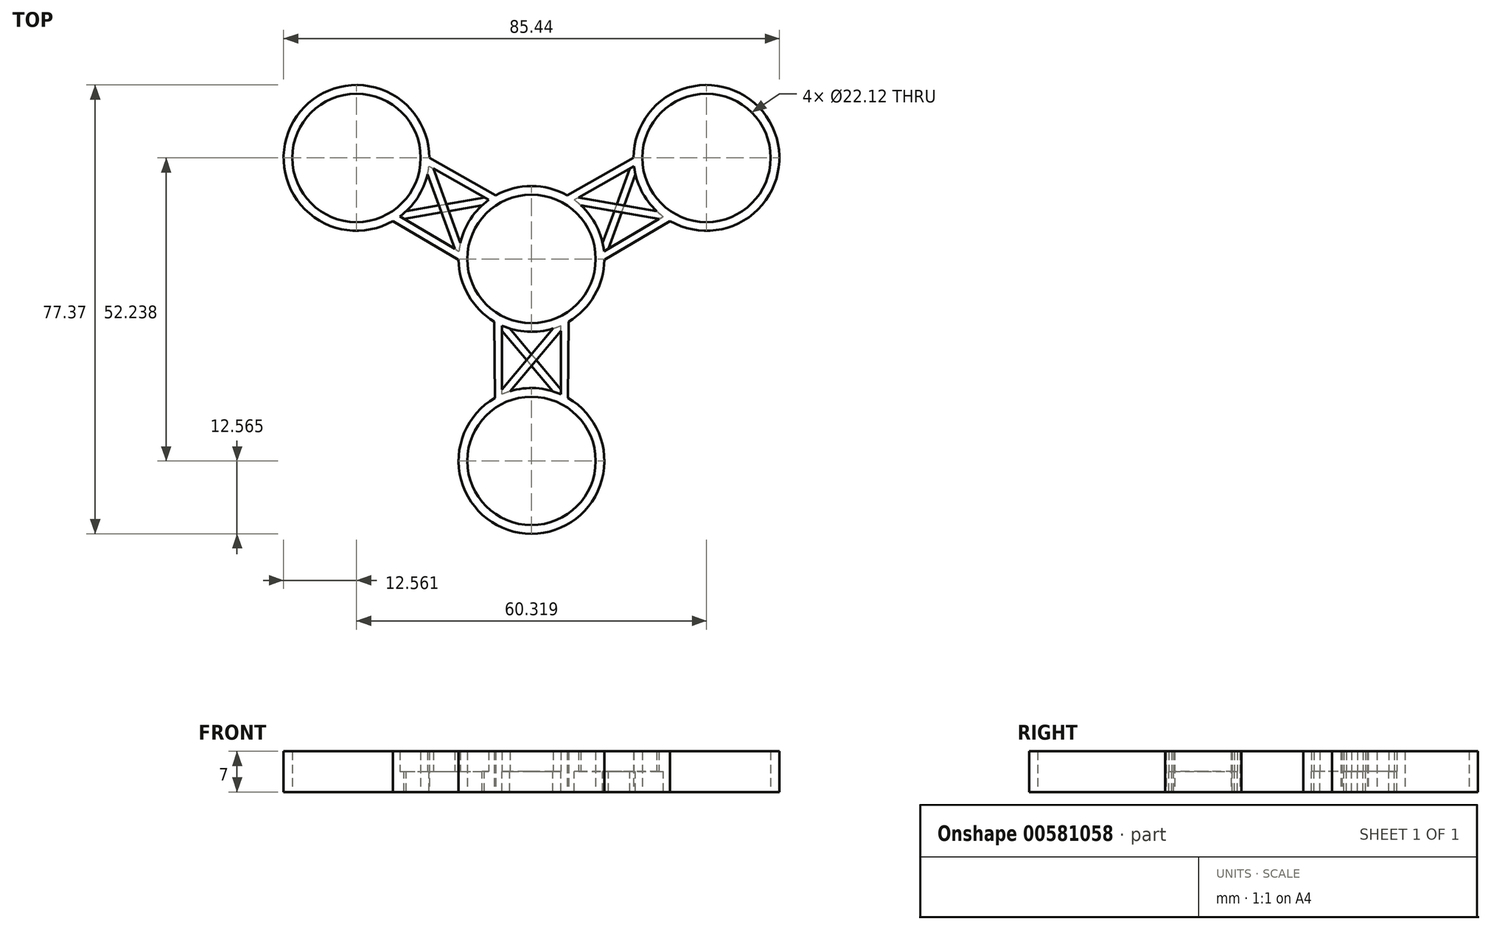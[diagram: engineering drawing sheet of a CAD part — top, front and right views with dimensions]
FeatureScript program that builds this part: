
annotation { "Feature Type Name" : "Feature", "Feature Type Description" : "" }
export const myFeature = defineFeature(function(context is Context, id is Id, definition is map)
    precondition{}
    {
        {
            var Q0;
            Q0=qCreatedBy(makeId("Top.planeOp"),FACE);
            var sketch = newSketch(context, id + "F0", { "sketchPlane" : qUnion([Q0])});
            skCircle(sketch, "E0", {"center": v(0, 0) * mm, "radius": 11.06 * mm});
            skCircle(sketch, "E1", {"center": v(-30.16, 17.41) * mm, "radius": 11.06 * mm});
            skCircle(sketch, "E2", {"center": v(0, -34.82) * mm, "radius": 11.06 * mm});
            skCircle(sketch, "E3", {"center": v(30.16, 17.41) * mm, "radius": 11.06 * mm});
            skLineSegment(sketch, "E4", {"start": v(-30.16, 17.41) * mm, "end": v(0, -34.82) * mm, "construction": true});
            skLineSegment(sketch, "E5", {"start": v(30.16, 17.41) * mm, "end": v(0, -34.82) * mm, "construction": true});
            skLineSegment(sketch, "E6", {"start": v(30.16, 17.41) * mm, "end": v(-30.16, 17.41) * mm, "construction": true});
            skCircle(sketch, "E7", {"center": v(0, 0) * mm, "radius": 12.56 * mm});
            skCircle(sketch, "E8", {"center": v(30.16, 17.41) * mm, "radius": 12.56 * mm});
            skCircle(sketch, "E9", {"center": v(-30.16, 17.41) * mm, "radius": 12.56 * mm});
            skCircle(sketch, "E10", {"center": v(0, -34.82) * mm, "radius": 12.56 * mm});
            skLineSegment(sketch, "E11", {"start": v(3.75, -11.99) * mm, "end": v(-6.28, -23.95) * mm});
            skLineSegment(sketch, "E12", {"start": v(-3.75, -11.99) * mm, "end": v(6.28, -23.95) * mm});
            skLineSegment(sketch, "E13", {"start": v(-3.67, -22.81) * mm, "end": v(6.4, -10.81) * mm});
            skLineSegment(sketch, "E14", {"start": v(-6.4, -10.81) * mm, "end": v(3.67, -22.81) * mm});
            skLineSegment(sketch, "E15", {"start": v(-17.6, 17.41) * mm, "end": v(-12.26, 2.75) * mm});
            skLineSegment(sketch, "E16", {"start": v(-23.88, 6.53) * mm, "end": v(-8.5, 9.24) * mm});
            skLineSegment(sketch, "E17", {"start": v(23.88, 6.53) * mm, "end": v(8.5, 9.24) * mm});
            skLineSegment(sketch, "E18", {"start": v(12.26, 2.75) * mm, "end": v(17.6, 17.41) * mm});
            skLineSegment(sketch, "E19", {"start": v(6.16, 10.95) * mm, "end": v(21.6, 8.23) * mm});
            skLineSegment(sketch, "E20", {"start": v(12.56, -0.13) * mm, "end": v(17.92, 14.58) * mm});
            skLineSegment(sketch, "E21", {"start": v(-17.92, 14.58) * mm, "end": v(-12.56, -0.13) * mm});
            skLineSegment(sketch, "E22", {"start": v(-21.6, 8.23) * mm, "end": v(-6.16, 10.95) * mm});
            skLineSegment(sketch, "E23", {"start": v(-23.88, 6.53) * mm, "end": v(-12.56, -0.13) * mm});
            skLineSegment(sketch, "E24", {"start": v(-17.6, 17.41) * mm, "end": v(-6.16, 10.95) * mm});
            skLineSegment(sketch, "E25", {"start": v(17.6, 17.41) * mm, "end": v(6.16, 10.95) * mm});
            skLineSegment(sketch, "E26", {"start": v(12.56, -0.13) * mm, "end": v(23.88, 6.53) * mm});
            skLineSegment(sketch, "E27", {"start": v(-6.28, -23.95) * mm, "end": v(-6.4, -10.81) * mm});
            skLineSegment(sketch, "E28", {"start": v(6.4, -10.81) * mm, "end": v(6.28, -23.95) * mm});
            skLineSegment(sketch, "E29", {"start": v(-22.7, 7.3) * mm, "end": v(-12.5, 1.3) * mm});
            skLineSegment(sketch, "E30", {"start": v(-17.68, 16) * mm, "end": v(-7.37, 10.17) * mm});
            skLineSegment(sketch, "E31", {"start": v(17.68, 16) * mm, "end": v(7.37, 10.17) * mm});
            skLineSegment(sketch, "E32", {"start": v(12.5, 1.3) * mm, "end": v(22.7, 7.3) * mm});
            skLineSegment(sketch, "E33", {"start": v(-5.07, -23.33) * mm, "end": v(-5.07, -11.5) * mm});
            skLineSegment(sketch, "E34", {"start": v(5.07, -23.33) * mm, "end": v(5.07, -11.5) * mm});
            skSolve(sketch);
        }
        {
            var Q0;
            Q0=makeQuery(id+"F0.imprint","IMPRINT",FACE,{"disambiguationData":[TD([[makeQuery(id+"F0.imprint","IMPRINT",EDGE,{"derivedFrom":sQuery(id+"F0.wireOp",EDGE,"E2")}),-1.0]])]});
            var Q1;
            Q1=makeQuery(id+"F0.imprint","IMPRINT",FACE,{"disambiguationData":[TD([[makeQuery(id+"F0.imprint","IMPRINT",EDGE,{"derivedFrom":sQuery(id+"F0.wireOp",EDGE,"E3")}),-1.0]])]});
            var Q2;
            Q2=makeQuery(id+"F0.imprint","IMPRINT",FACE,{"disambiguationData":[TD([[makeQuery(id+"F0.imprint","IMPRINT",EDGE,{"derivedFrom":sQuery(id+"F0.wireOp",EDGE,"E1")}),-1.0]])]});
            var Q3;
            Q3=makeQuery(id+"F0.imprint","IMPRINT",FACE,{"disambiguationData":[TD([[makeQuery(id+"F0.imprint","IMPRINT",EDGE,{"derivedFrom":sQuery(id+"F0.wireOp",EDGE,"E0")}),-1.0]])]});
            var Q4;
            {var subQ1=sQuery(id+"F0.wireOp",EDGE,"E9");var subQ3=sQuery(id+"F0.wireOp",EDGE,"E29");var subQ4=makeQuery(id+"F0.imprint","INTERSECT",VERTEX,{"derivedFrom":[subQ1,subQ3]});Q4=makeQuery(id+"F0.imprint","IMPRINT",FACE,{"disambiguationData":[TD([[makeQuery(id+"F0.imprint","IMPRINT",EDGE,{"disambiguationData":[TD([[subQ4,-1.0]])],"derivedFrom":subQ3}),-1.0]])]});}
            var Q5;
            {var subQ0=sQuery(id+"F0.wireOp",EDGE,"E23");Q5=makeQuery(id+"F0.imprint","IMPRINT",FACE,{"disambiguationData":[TD([[makeQuery(id+"F0.imprint","IMPRINT",EDGE,{"derivedFrom":subQ0}),1.0]])]});}
            var Q6;
            {var subQ1=sQuery(id+"F0.wireOp",EDGE,"E7");var subQ3=sQuery(id+"F0.wireOp",EDGE,"E29");var subQ4=makeQuery(id+"F0.imprint","INTERSECT",VERTEX,{"derivedFrom":[subQ1,subQ3]});Q6=makeQuery(id+"F0.imprint","IMPRINT",FACE,{"disambiguationData":[TD([[makeQuery(id+"F0.imprint","IMPRINT",EDGE,{"disambiguationData":[TD([[subQ4,1.0]])],"derivedFrom":subQ3}),-1.0]])]});}
            var Q7;
            {var subQ0=sQuery(id+"F0.wireOp",EDGE,"E24");Q7=makeQuery(id+"F0.imprint","IMPRINT",FACE,{"disambiguationData":[TD([[makeQuery(id+"F0.imprint","IMPRINT",EDGE,{"derivedFrom":subQ0}),-1.0]])]});}
            var Q8;
            {var subQ1=sQuery(id+"F0.wireOp",EDGE,"E9");var subQ3=sQuery(id+"F0.wireOp",EDGE,"E30");var subQ4=makeQuery(id+"F0.imprint","INTERSECT",VERTEX,{"derivedFrom":[subQ1,subQ3]});Q8=makeQuery(id+"F0.imprint","IMPRINT",FACE,{"disambiguationData":[TD([[makeQuery(id+"F0.imprint","IMPRINT",EDGE,{"disambiguationData":[TD([[subQ4,-1.0]])],"derivedFrom":subQ3}),1.0]])]});}
            var Q9;
            {var subQ1=sQuery(id+"F0.wireOp",EDGE,"E7");var subQ3=sQuery(id+"F0.wireOp",EDGE,"E30");var subQ4=makeQuery(id+"F0.imprint","INTERSECT",VERTEX,{"derivedFrom":[subQ1,subQ3]});Q9=makeQuery(id+"F0.imprint","IMPRINT",FACE,{"disambiguationData":[TD([[makeQuery(id+"F0.imprint","IMPRINT",EDGE,{"disambiguationData":[TD([[subQ4,1.0]])],"derivedFrom":subQ3}),1.0]])]});}
            var Q10;
            {var subQ1=sQuery(id+"F0.wireOp",EDGE,"E10");var subQ3=sQuery(id+"F0.wireOp",EDGE,"E33");var subQ4=makeQuery(id+"F0.imprint","INTERSECT",VERTEX,{"derivedFrom":[subQ1,subQ3]});Q10=makeQuery(id+"F0.imprint","IMPRINT",FACE,{"disambiguationData":[TD([[makeQuery(id+"F0.imprint","IMPRINT",EDGE,{"disambiguationData":[TD([[subQ4,-1.0]])],"derivedFrom":subQ3}),1.0]])]});}
            var Q11;
            {var subQ0=sQuery(id+"F0.wireOp",EDGE,"E27");Q11=makeQuery(id+"F0.imprint","IMPRINT",FACE,{"disambiguationData":[TD([[makeQuery(id+"F0.imprint","IMPRINT",EDGE,{"derivedFrom":subQ0}),-1.0]])]});}
            var Q12;
            {var subQ1=sQuery(id+"F0.wireOp",EDGE,"E7");var subQ3=sQuery(id+"F0.wireOp",EDGE,"E33");var subQ4=makeQuery(id+"F0.imprint","INTERSECT",VERTEX,{"derivedFrom":[subQ1,subQ3]});Q12=makeQuery(id+"F0.imprint","IMPRINT",FACE,{"disambiguationData":[TD([[makeQuery(id+"F0.imprint","IMPRINT",EDGE,{"disambiguationData":[TD([[subQ4,1.0]])],"derivedFrom":subQ3}),1.0]])]});}
            var Q13;
            {var subQ1=sQuery(id+"F0.wireOp",EDGE,"E7");var subQ3=sQuery(id+"F0.wireOp",EDGE,"E34");var subQ4=makeQuery(id+"F0.imprint","INTERSECT",VERTEX,{"derivedFrom":[subQ1,subQ3]});Q13=makeQuery(id+"F0.imprint","IMPRINT",FACE,{"disambiguationData":[TD([[makeQuery(id+"F0.imprint","IMPRINT",EDGE,{"disambiguationData":[TD([[subQ4,1.0]])],"derivedFrom":subQ3}),-1.0]])]});}
            var Q14;
            {var subQ0=sQuery(id+"F0.wireOp",EDGE,"E28");Q14=makeQuery(id+"F0.imprint","IMPRINT",FACE,{"disambiguationData":[TD([[makeQuery(id+"F0.imprint","IMPRINT",EDGE,{"derivedFrom":subQ0}),-1.0]])]});}
            var Q15;
            {var subQ1=sQuery(id+"F0.wireOp",EDGE,"E10");var subQ3=sQuery(id+"F0.wireOp",EDGE,"E34");var subQ4=makeQuery(id+"F0.imprint","INTERSECT",VERTEX,{"derivedFrom":[subQ1,subQ3]});Q15=makeQuery(id+"F0.imprint","IMPRINT",FACE,{"disambiguationData":[TD([[makeQuery(id+"F0.imprint","IMPRINT",EDGE,{"disambiguationData":[TD([[subQ4,-1.0]])],"derivedFrom":subQ3}),-1.0]])]});}
            var Q16;
            {var subQ3=sQuery(id+"F0.wireOp",EDGE,"E13");var subQ5=sQuery(id+"F0.wireOp",EDGE,"E10");var subQ6=makeQuery(id+"F0.imprint","INTERSECT",VERTEX,{"derivedFrom":[subQ5,subQ3]});Q16=makeQuery(id+"F0.imprint","IMPRINT",FACE,{"disambiguationData":[TD([[makeQuery(id+"F0.imprint","IMPRINT",EDGE,{"disambiguationData":[TD([[subQ6,-1.0]])],"derivedFrom":subQ5}),-1.0]])]});}
            var Q17;
            {var subQ0=sQuery(id+"F0.wireOp",EDGE,"E12");var subQ1=sQuery(id+"F0.wireOp",EDGE,"E11");var subQ2=makeQuery(id+"F0.imprint","INTERSECT",VERTEX,{"derivedFrom":[subQ1,subQ0]});Q17=makeQuery(id+"F0.imprint","IMPRINT",FACE,{"disambiguationData":[TD([[makeQuery(id+"F0.imprint","IMPRINT",EDGE,{"disambiguationData":[TD([[subQ2,-1.0]])],"derivedFrom":subQ1}),1.0]])]});}
            var Q18;
            {var subQ5=sQuery(id+"F0.wireOp",EDGE,"E11");var subQ7=sQuery(id+"F0.wireOp",EDGE,"E7");var subQ9=makeQuery(id+"F0.imprint","INTERSECT",VERTEX,{"derivedFrom":[subQ7,subQ5]});Q18=makeQuery(id+"F0.imprint","IMPRINT",FACE,{"disambiguationData":[TD([[makeQuery(id+"F0.imprint","IMPRINT",EDGE,{"disambiguationData":[TD([[subQ9,-1.0]])],"derivedFrom":subQ7}),-1.0]])]});}
            var Q19;
            {var subQ0=sQuery(id+"F0.wireOp",EDGE,"E26");Q19=makeQuery(id+"F0.imprint","IMPRINT",FACE,{"disambiguationData":[TD([[makeQuery(id+"F0.imprint","IMPRINT",EDGE,{"derivedFrom":subQ0}),1.0]])]});}
            var Q20;
            {var subQ1=sQuery(id+"F0.wireOp",EDGE,"E7");var subQ3=sQuery(id+"F0.wireOp",EDGE,"E32");var subQ4=makeQuery(id+"F0.imprint","INTERSECT",VERTEX,{"derivedFrom":[subQ1,subQ3]});Q20=makeQuery(id+"F0.imprint","IMPRINT",FACE,{"disambiguationData":[TD([[makeQuery(id+"F0.imprint","IMPRINT",EDGE,{"disambiguationData":[TD([[subQ4,-1.0]])],"derivedFrom":subQ3}),-1.0]])]});}
            var Q21;
            {var subQ1=sQuery(id+"F0.wireOp",EDGE,"E8");var subQ3=sQuery(id+"F0.wireOp",EDGE,"E32");var subQ4=makeQuery(id+"F0.imprint","INTERSECT",VERTEX,{"derivedFrom":[subQ1,subQ3]});Q21=makeQuery(id+"F0.imprint","IMPRINT",FACE,{"disambiguationData":[TD([[makeQuery(id+"F0.imprint","IMPRINT",EDGE,{"disambiguationData":[TD([[subQ4,1.0]])],"derivedFrom":subQ3}),-1.0]])]});}
            var Q22;
            {var subQ0=sQuery(id+"F0.wireOp",EDGE,"E25");Q22=makeQuery(id+"F0.imprint","IMPRINT",FACE,{"disambiguationData":[TD([[makeQuery(id+"F0.imprint","IMPRINT",EDGE,{"derivedFrom":subQ0}),1.0]])]});}
            var Q23;
            {var subQ1=sQuery(id+"F0.wireOp",EDGE,"E7");var subQ3=sQuery(id+"F0.wireOp",EDGE,"E31");var subQ4=makeQuery(id+"F0.imprint","INTERSECT",VERTEX,{"derivedFrom":[subQ1,subQ3]});Q23=makeQuery(id+"F0.imprint","IMPRINT",FACE,{"disambiguationData":[TD([[makeQuery(id+"F0.imprint","IMPRINT",EDGE,{"disambiguationData":[TD([[subQ4,1.0]])],"derivedFrom":subQ3}),-1.0]])]});}
            var Q24;
            {var subQ1=sQuery(id+"F0.wireOp",EDGE,"E8");var subQ3=sQuery(id+"F0.wireOp",EDGE,"E31");var subQ4=makeQuery(id+"F0.imprint","INTERSECT",VERTEX,{"derivedFrom":[subQ1,subQ3]});Q24=makeQuery(id+"F0.imprint","IMPRINT",FACE,{"disambiguationData":[TD([[makeQuery(id+"F0.imprint","IMPRINT",EDGE,{"disambiguationData":[TD([[subQ4,-1.0]])],"derivedFrom":subQ3}),-1.0]])]});}
            var Q25;
            {var subQ3=sQuery(id+"F0.wireOp",EDGE,"E19");var subQ5=sQuery(id+"F0.wireOp",EDGE,"E8");var subQ6=makeQuery(id+"F0.imprint","INTERSECT",VERTEX,{"derivedFrom":[subQ5,subQ3]});Q25=makeQuery(id+"F0.imprint","IMPRINT",FACE,{"disambiguationData":[TD([[makeQuery(id+"F0.imprint","IMPRINT",EDGE,{"disambiguationData":[TD([[subQ6,-1.0]])],"derivedFrom":subQ5}),-1.0]])]});}
            var Q26;
            {var subQ0=sQuery(id+"F0.wireOp",EDGE,"E20");var subQ1=sQuery(id+"F0.wireOp",EDGE,"E17");var subQ2=makeQuery(id+"F0.imprint","INTERSECT",VERTEX,{"derivedFrom":[subQ1,subQ0]});Q26=makeQuery(id+"F0.imprint","IMPRINT",FACE,{"disambiguationData":[TD([[makeQuery(id+"F0.imprint","IMPRINT",EDGE,{"disambiguationData":[TD([[subQ2,-1.0]])],"derivedFrom":subQ1}),-1.0]])]});}
            var Q27;
            {var subQ5=sQuery(id+"F0.wireOp",EDGE,"E17");var subQ7=sQuery(id+"F0.wireOp",EDGE,"E7");var subQ9=makeQuery(id+"F0.imprint","INTERSECT",VERTEX,{"derivedFrom":[subQ7,subQ5]});Q27=makeQuery(id+"F0.imprint","IMPRINT",FACE,{"disambiguationData":[TD([[makeQuery(id+"F0.imprint","IMPRINT",EDGE,{"disambiguationData":[TD([[subQ9,-1.0]])],"derivedFrom":subQ7}),-1.0]])]});}
            var Q28;
            {var subQ3=sQuery(id+"F0.wireOp",EDGE,"E21");var subQ5=sQuery(id+"F0.wireOp",EDGE,"E9");var subQ6=makeQuery(id+"F0.imprint","INTERSECT",VERTEX,{"derivedFrom":[subQ5,subQ3]});Q28=makeQuery(id+"F0.imprint","IMPRINT",FACE,{"disambiguationData":[TD([[makeQuery(id+"F0.imprint","IMPRINT",EDGE,{"disambiguationData":[TD([[subQ6,-1.0]])],"derivedFrom":subQ5}),-1.0]])]});}
            var Q29;
            {var subQ0=sQuery(id+"F0.wireOp",EDGE,"E22");var subQ1=sQuery(id+"F0.wireOp",EDGE,"E15");var subQ2=makeQuery(id+"F0.imprint","INTERSECT",VERTEX,{"derivedFrom":[subQ1,subQ0]});Q29=makeQuery(id+"F0.imprint","IMPRINT",FACE,{"disambiguationData":[TD([[makeQuery(id+"F0.imprint","IMPRINT",EDGE,{"disambiguationData":[TD([[subQ2,-1.0]])],"derivedFrom":subQ1}),-1.0]])]});}
            var Q30;
            {var subQ0=sQuery(id+"F0.wireOp",EDGE,"E15");var subQ1=sQuery(id+"F0.wireOp",EDGE,"E7");var subQ2=makeQuery(id+"F0.imprint","INTERSECT",VERTEX,{"derivedFrom":[subQ1,subQ0]});Q30=makeQuery(id+"F0.imprint","IMPRINT",FACE,{"disambiguationData":[TD([[makeQuery(id+"F0.imprint","IMPRINT",EDGE,{"disambiguationData":[TD([[subQ2,-1.0]])],"derivedFrom":subQ1}),-1.0]])]});}
            extrude(context, id + "F1", {"entities" : qUnion([Q0, Q1, Q2, Q3, Q4, Q5, Q6, Q7, Q8, Q9, Q10, Q11, Q12, Q13, Q14, Q15, Q16, Q17, Q18, Q19, Q20, Q21, Q22, Q23, Q24, Q25, Q26, Q27, Q28, Q29, Q30]), "depth" : 3.5 * mm, "offsetDistance" : 25.4 * mm});
        }
        {
            var Q0;
            {var subQ1=sQuery(id+"F0.wireOp",EDGE,"E7");var subQ3=sQuery(id+"F0.wireOp",EDGE,"E29");var subQ4=makeQuery(id+"F0.imprint","INTERSECT",VERTEX,{"derivedFrom":[subQ1,subQ3]});Q0=makeQuery(id+"F0.imprint","IMPRINT",FACE,{"disambiguationData":[TD([[makeQuery(id+"F0.imprint","IMPRINT",EDGE,{"disambiguationData":[TD([[subQ4,1.0]])],"derivedFrom":subQ3}),-1.0]])]});}
            var Q1;
            {var subQ0=sQuery(id+"F0.wireOp",EDGE,"E23");Q1=makeQuery(id+"F0.imprint","IMPRINT",FACE,{"disambiguationData":[TD([[makeQuery(id+"F0.imprint","IMPRINT",EDGE,{"derivedFrom":subQ0}),1.0]])]});}
            var Q2;
            {var subQ1=sQuery(id+"F0.wireOp",EDGE,"E9");var subQ3=sQuery(id+"F0.wireOp",EDGE,"E29");var subQ4=makeQuery(id+"F0.imprint","INTERSECT",VERTEX,{"derivedFrom":[subQ1,subQ3]});Q2=makeQuery(id+"F0.imprint","IMPRINT",FACE,{"disambiguationData":[TD([[makeQuery(id+"F0.imprint","IMPRINT",EDGE,{"disambiguationData":[TD([[subQ4,-1.0]])],"derivedFrom":subQ3}),-1.0]])]});}
            var Q3;
            Q3=makeQuery(id+"F0.imprint","IMPRINT",FACE,{"disambiguationData":[TD([[makeQuery(id+"F0.imprint","IMPRINT",EDGE,{"derivedFrom":sQuery(id+"F0.wireOp",EDGE,"E1")}),-1.0]])]});
            var Q4;
            {var subQ1=sQuery(id+"F0.wireOp",EDGE,"E9");var subQ3=sQuery(id+"F0.wireOp",EDGE,"E30");var subQ4=makeQuery(id+"F0.imprint","INTERSECT",VERTEX,{"derivedFrom":[subQ1,subQ3]});Q4=makeQuery(id+"F0.imprint","IMPRINT",FACE,{"disambiguationData":[TD([[makeQuery(id+"F0.imprint","IMPRINT",EDGE,{"disambiguationData":[TD([[subQ4,-1.0]])],"derivedFrom":subQ3}),1.0]])]});}
            var Q5;
            {var subQ0=sQuery(id+"F0.wireOp",EDGE,"E24");Q5=makeQuery(id+"F0.imprint","IMPRINT",FACE,{"disambiguationData":[TD([[makeQuery(id+"F0.imprint","IMPRINT",EDGE,{"derivedFrom":subQ0}),-1.0]])]});}
            var Q6;
            {var subQ1=sQuery(id+"F0.wireOp",EDGE,"E7");var subQ3=sQuery(id+"F0.wireOp",EDGE,"E30");var subQ4=makeQuery(id+"F0.imprint","INTERSECT",VERTEX,{"derivedFrom":[subQ1,subQ3]});Q6=makeQuery(id+"F0.imprint","IMPRINT",FACE,{"disambiguationData":[TD([[makeQuery(id+"F0.imprint","IMPRINT",EDGE,{"disambiguationData":[TD([[subQ4,1.0]])],"derivedFrom":subQ3}),1.0]])]});}
            var Q7;
            Q7=makeQuery(id+"F0.imprint","IMPRINT",FACE,{"disambiguationData":[TD([[makeQuery(id+"F0.imprint","IMPRINT",EDGE,{"derivedFrom":sQuery(id+"F0.wireOp",EDGE,"E3")}),-1.0]])]});
            var Q8;
            {var subQ1=sQuery(id+"F0.wireOp",EDGE,"E8");var subQ3=sQuery(id+"F0.wireOp",EDGE,"E31");var subQ4=makeQuery(id+"F0.imprint","INTERSECT",VERTEX,{"derivedFrom":[subQ1,subQ3]});Q8=makeQuery(id+"F0.imprint","IMPRINT",FACE,{"disambiguationData":[TD([[makeQuery(id+"F0.imprint","IMPRINT",EDGE,{"disambiguationData":[TD([[subQ4,-1.0]])],"derivedFrom":subQ3}),-1.0]])]});}
            var Q9;
            {var subQ0=sQuery(id+"F0.wireOp",EDGE,"E25");Q9=makeQuery(id+"F0.imprint","IMPRINT",FACE,{"disambiguationData":[TD([[makeQuery(id+"F0.imprint","IMPRINT",EDGE,{"derivedFrom":subQ0}),1.0]])]});}
            var Q10;
            {var subQ1=sQuery(id+"F0.wireOp",EDGE,"E7");var subQ3=sQuery(id+"F0.wireOp",EDGE,"E31");var subQ4=makeQuery(id+"F0.imprint","INTERSECT",VERTEX,{"derivedFrom":[subQ1,subQ3]});Q10=makeQuery(id+"F0.imprint","IMPRINT",FACE,{"disambiguationData":[TD([[makeQuery(id+"F0.imprint","IMPRINT",EDGE,{"disambiguationData":[TD([[subQ4,1.0]])],"derivedFrom":subQ3}),-1.0]])]});}
            var Q11;
            {var subQ0=sQuery(id+"F0.wireOp",EDGE,"E26");Q11=makeQuery(id+"F0.imprint","IMPRINT",FACE,{"disambiguationData":[TD([[makeQuery(id+"F0.imprint","IMPRINT",EDGE,{"derivedFrom":subQ0}),1.0]])]});}
            var Q12;
            {var subQ1=sQuery(id+"F0.wireOp",EDGE,"E8");var subQ3=sQuery(id+"F0.wireOp",EDGE,"E32");var subQ4=makeQuery(id+"F0.imprint","INTERSECT",VERTEX,{"derivedFrom":[subQ1,subQ3]});Q12=makeQuery(id+"F0.imprint","IMPRINT",FACE,{"disambiguationData":[TD([[makeQuery(id+"F0.imprint","IMPRINT",EDGE,{"disambiguationData":[TD([[subQ4,1.0]])],"derivedFrom":subQ3}),-1.0]])]});}
            var Q13;
            {var subQ1=sQuery(id+"F0.wireOp",EDGE,"E7");var subQ3=sQuery(id+"F0.wireOp",EDGE,"E32");var subQ4=makeQuery(id+"F0.imprint","INTERSECT",VERTEX,{"derivedFrom":[subQ1,subQ3]});Q13=makeQuery(id+"F0.imprint","IMPRINT",FACE,{"disambiguationData":[TD([[makeQuery(id+"F0.imprint","IMPRINT",EDGE,{"disambiguationData":[TD([[subQ4,-1.0]])],"derivedFrom":subQ3}),-1.0]])]});}
            var Q14;
            Q14=makeQuery(id+"F0.imprint","IMPRINT",FACE,{"disambiguationData":[TD([[makeQuery(id+"F0.imprint","IMPRINT",EDGE,{"derivedFrom":sQuery(id+"F0.wireOp",EDGE,"E2")}),-1.0]])]});
            var Q15;
            {var subQ1=sQuery(id+"F0.wireOp",EDGE,"E10");var subQ3=sQuery(id+"F0.wireOp",EDGE,"E34");var subQ4=makeQuery(id+"F0.imprint","INTERSECT",VERTEX,{"derivedFrom":[subQ1,subQ3]});Q15=makeQuery(id+"F0.imprint","IMPRINT",FACE,{"disambiguationData":[TD([[makeQuery(id+"F0.imprint","IMPRINT",EDGE,{"disambiguationData":[TD([[subQ4,-1.0]])],"derivedFrom":subQ3}),-1.0]])]});}
            var Q16;
            {var subQ1=sQuery(id+"F0.wireOp",EDGE,"E10");var subQ3=sQuery(id+"F0.wireOp",EDGE,"E33");var subQ4=makeQuery(id+"F0.imprint","INTERSECT",VERTEX,{"derivedFrom":[subQ1,subQ3]});Q16=makeQuery(id+"F0.imprint","IMPRINT",FACE,{"disambiguationData":[TD([[makeQuery(id+"F0.imprint","IMPRINT",EDGE,{"disambiguationData":[TD([[subQ4,-1.0]])],"derivedFrom":subQ3}),1.0]])]});}
            var Q17;
            {var subQ0=sQuery(id+"F0.wireOp",EDGE,"E27");Q17=makeQuery(id+"F0.imprint","IMPRINT",FACE,{"disambiguationData":[TD([[makeQuery(id+"F0.imprint","IMPRINT",EDGE,{"derivedFrom":subQ0}),-1.0]])]});}
            var Q18;
            {var subQ0=sQuery(id+"F0.wireOp",EDGE,"E28");Q18=makeQuery(id+"F0.imprint","IMPRINT",FACE,{"disambiguationData":[TD([[makeQuery(id+"F0.imprint","IMPRINT",EDGE,{"derivedFrom":subQ0}),-1.0]])]});}
            var Q19;
            {var subQ1=sQuery(id+"F0.wireOp",EDGE,"E7");var subQ3=sQuery(id+"F0.wireOp",EDGE,"E33");var subQ4=makeQuery(id+"F0.imprint","INTERSECT",VERTEX,{"derivedFrom":[subQ1,subQ3]});Q19=makeQuery(id+"F0.imprint","IMPRINT",FACE,{"disambiguationData":[TD([[makeQuery(id+"F0.imprint","IMPRINT",EDGE,{"disambiguationData":[TD([[subQ4,1.0]])],"derivedFrom":subQ3}),1.0]])]});}
            var Q20;
            {var subQ1=sQuery(id+"F0.wireOp",EDGE,"E7");var subQ3=sQuery(id+"F0.wireOp",EDGE,"E34");var subQ4=makeQuery(id+"F0.imprint","INTERSECT",VERTEX,{"derivedFrom":[subQ1,subQ3]});Q20=makeQuery(id+"F0.imprint","IMPRINT",FACE,{"disambiguationData":[TD([[makeQuery(id+"F0.imprint","IMPRINT",EDGE,{"disambiguationData":[TD([[subQ4,1.0]])],"derivedFrom":subQ3}),-1.0]])]});}
            var Q21;
            Q21=makeQuery(id+"F0.imprint","IMPRINT",FACE,{"disambiguationData":[TD([[makeQuery(id+"F0.imprint","IMPRINT",EDGE,{"derivedFrom":sQuery(id+"F0.wireOp",EDGE,"E0")}),-1.0]])]});
            var Q22;
            {var subQ3=sQuery(id+"F0.wireOp",EDGE,"E14");var subQ7=sQuery(id+"F0.wireOp",EDGE,"E10");var subQ8=makeQuery(id+"F0.imprint","INTERSECT",VERTEX,{"derivedFrom":[subQ7,subQ3]});Q22=makeQuery(id+"F0.imprint","IMPRINT",FACE,{"disambiguationData":[TD([[makeQuery(id+"F0.imprint","IMPRINT",EDGE,{"disambiguationData":[TD([[subQ8,1.0]])],"derivedFrom":subQ7}),-1.0]])]});}
            var Q23;
            {var subQ0=sQuery(id+"F0.wireOp",EDGE,"E12");var subQ1=sQuery(id+"F0.wireOp",EDGE,"E11");var subQ2=makeQuery(id+"F0.imprint","INTERSECT",VERTEX,{"derivedFrom":[subQ1,subQ0]});Q23=makeQuery(id+"F0.imprint","IMPRINT",FACE,{"disambiguationData":[TD([[makeQuery(id+"F0.imprint","IMPRINT",EDGE,{"disambiguationData":[TD([[subQ2,-1.0]])],"derivedFrom":subQ1}),1.0]])]});}
            var Q24;
            {var subQ5=sQuery(id+"F0.wireOp",EDGE,"E7");var subQ7=sQuery(id+"F0.wireOp",EDGE,"E12");var subQ8=makeQuery(id+"F0.imprint","INTERSECT",VERTEX,{"derivedFrom":[subQ5,subQ7]});Q24=makeQuery(id+"F0.imprint","IMPRINT",FACE,{"disambiguationData":[TD([[makeQuery(id+"F0.imprint","IMPRINT",EDGE,{"disambiguationData":[TD([[subQ8,1.0]])],"derivedFrom":subQ5}),-1.0]])]});}
            var Q25;
            {var subQ0=sQuery(id+"F0.wireOp",EDGE,"E20");var subQ1=sQuery(id+"F0.wireOp",EDGE,"E8");var subQ2=makeQuery(id+"F0.imprint","INTERSECT",VERTEX,{"derivedFrom":[subQ1,subQ0]});Q25=makeQuery(id+"F0.imprint","IMPRINT",FACE,{"disambiguationData":[TD([[makeQuery(id+"F0.imprint","IMPRINT",EDGE,{"disambiguationData":[TD([[subQ2,1.0]])],"derivedFrom":subQ1}),-1.0]])]});}
            var Q26;
            {var subQ0=sQuery(id+"F0.wireOp",EDGE,"E20");var subQ1=sQuery(id+"F0.wireOp",EDGE,"E17");var subQ2=makeQuery(id+"F0.imprint","INTERSECT",VERTEX,{"derivedFrom":[subQ1,subQ0]});Q26=makeQuery(id+"F0.imprint","IMPRINT",FACE,{"disambiguationData":[TD([[makeQuery(id+"F0.imprint","IMPRINT",EDGE,{"disambiguationData":[TD([[subQ2,-1.0]])],"derivedFrom":subQ1}),-1.0]])]});}
            var Q27;
            {var subQ5=sQuery(id+"F0.wireOp",EDGE,"E18");var subQ7=sQuery(id+"F0.wireOp",EDGE,"E7");var subQ8=makeQuery(id+"F0.imprint","INTERSECT",VERTEX,{"derivedFrom":[subQ7,subQ5]});Q27=makeQuery(id+"F0.imprint","IMPRINT",FACE,{"disambiguationData":[TD([[makeQuery(id+"F0.imprint","IMPRINT",EDGE,{"disambiguationData":[TD([[subQ8,1.0]])],"derivedFrom":subQ7}),-1.0]])]});}
            var Q28;
            {var subQ0=sQuery(id+"F0.wireOp",EDGE,"E22");var subQ1=sQuery(id+"F0.wireOp",EDGE,"E9");var subQ2=makeQuery(id+"F0.imprint","INTERSECT",VERTEX,{"derivedFrom":[subQ1,subQ0]});Q28=makeQuery(id+"F0.imprint","IMPRINT",FACE,{"disambiguationData":[TD([[makeQuery(id+"F0.imprint","IMPRINT",EDGE,{"disambiguationData":[TD([[subQ2,1.0]])],"derivedFrom":subQ1}),-1.0]])]});}
            var Q29;
            {var subQ0=sQuery(id+"F0.wireOp",EDGE,"E22");var subQ1=sQuery(id+"F0.wireOp",EDGE,"E15");var subQ2=makeQuery(id+"F0.imprint","INTERSECT",VERTEX,{"derivedFrom":[subQ1,subQ0]});Q29=makeQuery(id+"F0.imprint","IMPRINT",FACE,{"disambiguationData":[TD([[makeQuery(id+"F0.imprint","IMPRINT",EDGE,{"disambiguationData":[TD([[subQ2,-1.0]])],"derivedFrom":subQ1}),-1.0]])]});}
            var Q30;
            {var subQ5=sQuery(id+"F0.wireOp",EDGE,"E16");var subQ6=sQuery(id+"F0.wireOp",EDGE,"E7");var subQ7=makeQuery(id+"F0.imprint","INTERSECT",VERTEX,{"derivedFrom":[subQ6,subQ5]});Q30=makeQuery(id+"F0.imprint","IMPRINT",FACE,{"disambiguationData":[TD([[makeQuery(id+"F0.imprint","IMPRINT",EDGE,{"disambiguationData":[TD([[subQ7,1.0]])],"derivedFrom":subQ6}),-1.0]])]});}
            extrude(context, id + "F2", {"entities" : qUnion([Q0, Q1, Q2, Q3, Q4, Q5, Q6, Q7, Q8, Q9, Q10, Q11, Q12, Q13, Q14, Q15, Q16, Q17, Q18, Q19, Q20, Q21, Q22, Q23, Q24, Q25, Q26, Q27, Q28, Q29, Q30]), "operationType" : NewBodyOperationType.ADD, "oppositeDirection" : true, "depth" : 3.5 * mm, "offsetDistance" : 25.4 * mm});
        }
    });
